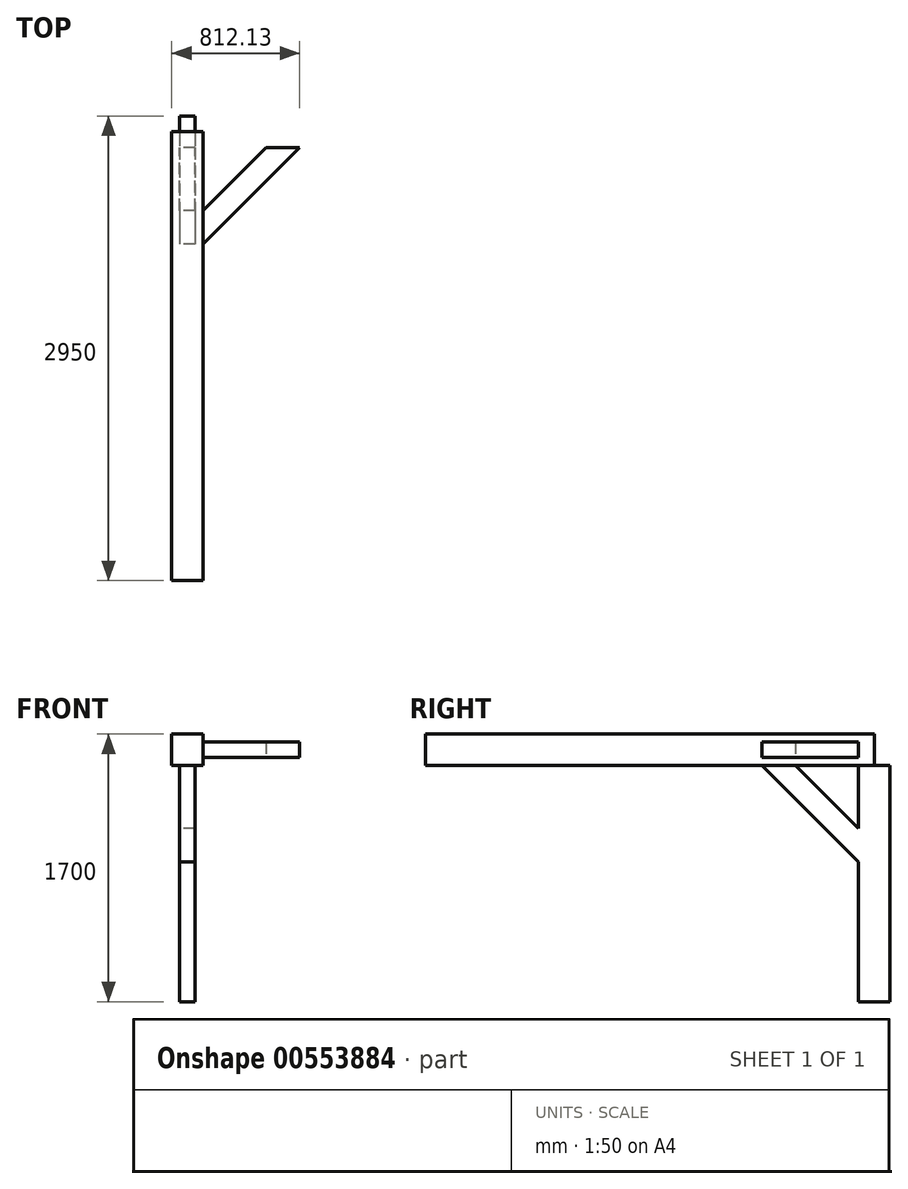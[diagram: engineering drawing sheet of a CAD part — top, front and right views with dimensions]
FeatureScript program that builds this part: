
annotation { "Feature Type Name" : "Feature", "Feature Type Description" : "" }
export const myFeature = defineFeature(function(context is Context, id is Id, definition is map)
    precondition{}
    {
        {
            var Q0;
            Q0=qCreatedBy(makeId("Top.planeOp"),FACE);
            var sketch = newSketch(context, id + "F0", { "sketchPlane" : qUnion([Q0])});
            skLineSegment(sketch, "E0", {"start": v(-358.87, -1603.5) * mm, "end": v(-158.87, -1603.5) * mm});
            skLineSegment(sketch, "E1", {"start": v(-158.87, -1603.5) * mm, "end": v(-158.87, 534.37) * mm});
            skLineSegment(sketch, "E2", {"start": v(-158.87, 534.37) * mm, "end": v(453.26, 1146.5) * mm});
            skLineSegment(sketch, "E3", {"start": v(453.26, 1146.5) * mm, "end": v(241.13, 1146.5) * mm});
            skLineSegment(sketch, "E4", {"start": v(241.13, 1146.5) * mm, "end": v(-158.87, 746.5) * mm});
            skLineSegment(sketch, "E5", {"start": v(-158.87, 746.5) * mm, "end": v(-158.87, 1246.5) * mm});
            skLineSegment(sketch, "E6", {"start": v(-158.87, 1246.5) * mm, "end": v(-358.87, 1246.5) * mm});
            skLineSegment(sketch, "E7", {"start": v(-358.87, 1246.5) * mm, "end": v(-358.87, -1603.5) * mm});
            skSolve(sketch);
        }
        {
            var Q0;
            Q0=makeQuery(id+"F0.imprint","IMPRINT",FACE,{"disambiguationData":[TD([[makeQuery(id+"F0.imprint","IMPRINT",EDGE,{"derivedFrom":sQuery(id+"F0.wireOp",EDGE,"E0")}),1.0]])]});
            extrude(context, id + "F1", {"entities" : qUnion([Q0]), "depth" : 200 * mm});
        }
        {
            var Q0;
            Q0=makeQuery(id+"F1.opExtrude","CAP_FACE",FACE,{"disambiguationData":[OSD([sQuery(id+"F0.wireOp",EDGE,"E0"),sQuery(id+"F0.wireOp",EDGE,"E1"),sQuery(id+"F0.wireOp",EDGE,"E2"),sQuery(id+"F0.wireOp",EDGE,"E3"),sQuery(id+"F0.wireOp",EDGE,"E4"),sQuery(id+"F0.wireOp",EDGE,"E5"),sQuery(id+"F0.wireOp",EDGE,"E6"),sQuery(id+"F0.wireOp",EDGE,"E7")])],"isStart":true});
            var sketch = newSketch(context, id + "F2", { "sketchPlane" : qUnion([Q0])});
            skLineSegment(sketch, "E8", {"start": v(-158.87, -534.37) * mm, "end": v(-158.87, -746.5) * mm});
            skLineSegment(sketch, "E9", {"start": v(-158.87, -746.5) * mm, "end": v(241.13, -1146.5) * mm});
            skLineSegment(sketch, "E10", {"start": v(241.13, -1146.5) * mm, "end": v(453.26, -1146.5) * mm});
            skLineSegment(sketch, "E11", {"start": v(453.26, -1146.5) * mm, "end": v(-158.87, -534.37) * mm});
            skSolve(sketch);
        }
        {
            var Q0;
            Q0=makeQuery(id+"F2.imprint","IMPRINT",FACE,{"disambiguationData":[TD([[makeQuery(id+"F2.imprint","IMPRINT",EDGE,{"derivedFrom":sQuery(id+"F2.wireOp",EDGE,"E8")}),1.0]])]});
            extrude(context, id + "F3", {"entities" : qUnion([Q0]), "operationType" : NewBodyOperationType.REMOVE, "oppositeDirection" : true, "depth" : 50 * mm});
        }
        {
            var Q0;
            Q0=makeQuery(id+"F1.opExtrude","CAP_FACE",FACE,{"disambiguationData":[OSD([sQuery(id+"F0.wireOp",EDGE,"E0"),sQuery(id+"F0.wireOp",EDGE,"E1"),sQuery(id+"F0.wireOp",EDGE,"E2"),sQuery(id+"F0.wireOp",EDGE,"E3"),sQuery(id+"F0.wireOp",EDGE,"E4"),sQuery(id+"F0.wireOp",EDGE,"E5"),sQuery(id+"F0.wireOp",EDGE,"E6"),sQuery(id+"F0.wireOp",EDGE,"E7")])],"isStart":false});
            var sketch = newSketch(context, id + "F4", { "sketchPlane" : qUnion([Q0])});
            skLineSegment(sketch, "E12", {"start": v(-158.87, 746.5) * mm, "end": v(-158.87, 534.37) * mm});
            skLineSegment(sketch, "E13", {"start": v(-158.87, 534.37) * mm, "end": v(453.26, 1146.5) * mm});
            skLineSegment(sketch, "E14", {"start": v(453.26, 1146.5) * mm, "end": v(241.13, 1146.5) * mm});
            skLineSegment(sketch, "E15", {"start": v(241.13, 1146.5) * mm, "end": v(-158.87, 746.5) * mm});
            skSolve(sketch);
        }
        {
            var Q0;
            Q0=makeQuery(id+"F4.imprint","IMPRINT",FACE,{"disambiguationData":[TD([[makeQuery(id+"F4.imprint","IMPRINT",EDGE,{"derivedFrom":sQuery(id+"F4.wireOp",EDGE,"E12")}),1.0]])]});
            extrude(context, id + "F5", {"entities" : qUnion([Q0]), "operationType" : NewBodyOperationType.REMOVE, "oppositeDirection" : true, "depth" : 50 * mm});
        }
        {
            var Q0;
            Q0=makeQuery(id+"F1.opExtrude","SWEPT_FACE",FACE,{"disambiguationData":[OSD([sQuery(id+"F0.wireOp",EDGE,"E7")])]});
            cPlane(context, id + "F6", {"entities" : qUnion([Q0]), "cplaneType" : CPlaneType.OFFSET, "offset" : 50 * mm, "oppositeDirection" : true, "width" : 150 * mm, "height" : 150 * mm});
        }
        {
            var Q0;
            Q0=qCreatedBy(id+"F6.planeOp",FACE);
            var sketch = newSketch(context, id + "F7", { "sketchPlane" : qUnion([Q0])});
            skLineSegment(sketch, "E16.0", {"start": v(-1246.5, 0) * mm, "end": v(1603.5, 0) * mm});
            skLineSegment(sketch, "E17", {"start": v(-746.5, 0) * mm, "end": v(-1146.5, -400) * mm});
            skLineSegment(sketch, "E18", {"start": v(-1146.5, -400) * mm, "end": v(-1146.5, -612.13) * mm});
            skLineSegment(sketch, "E19", {"start": v(-1146.5, -612.13) * mm, "end": v(-534.37, 0) * mm});
            skLineSegment(sketch, "E20", {"start": v(-534.37, 0) * mm, "end": v(-746.5, 0) * mm});
            skSolve(sketch);
        }
        {
            var Q0;
            Q0=makeQuery(id+"F7.imprint","IMPRINT",FACE,{"disambiguationData":[TD([[makeQuery(id+"F7.imprint","IMPRINT",EDGE,{"derivedFrom":sQuery(id+"F7.wireOp",EDGE,"E17")}),1.0]])]});
            extrude(context, id + "F8", {"entities" : qUnion([Q0]), "operationType" : NewBodyOperationType.ADD, "oppositeDirection" : true, "depth" : 100 * mm});
        }
        {
            var Q0;
            Q0=makeQuery(id+"F8.opExtrude","SWEPT_FACE",FACE,{"disambiguationData":[OSD([sQuery(id+"F7.wireOp",EDGE,"E18")])]});
            var sketch = newSketch(context, id + "F9", { "sketchPlane" : qUnion([Q0])});
            skLineSegment(sketch, "E21.bottom", {"start": v(208.87, -1500) * mm, "end": v(308.87, -1500) * mm});
            skLineSegment(sketch, "E21.top", {"start": v(208.87, 0) * mm, "end": v(308.87, 0) * mm});
            skLineSegment(sketch, "E21.left", {"start": v(208.87, -1500) * mm, "end": v(208.87, 0) * mm});
            skLineSegment(sketch, "E21.right", {"start": v(308.87, -1500) * mm, "end": v(308.87, 0) * mm});
            skSolve(sketch);
        }
        {
            var Q0;
            {var subQ0=sQuery(id+"F9.wireOp",EDGE,"E21.bottom");Q0=makeQuery(id+"F9.imprint","IMPRINT",FACE,{"disambiguationData":[TD([[makeQuery(id+"F9.imprint","IMPRINT",EDGE,{"derivedFrom":subQ0}),1.0]])]});}
            var Q1;
            {var subQ1=sQuery(id+"F7.wireOp",EDGE,"E18");var subQ2=makeQuery(id+"F8.opExtrude","SWEPT_EDGE",EDGE,{"disambiguationData":[OSD([sQuery(id+"F7.wireOp",EDGE,"E17"),subQ1])]});Q1=makeQuery(id+"F9.imprint","IMPRINT",FACE,{"disambiguationData":[TD([[makeQuery(id+"F9.imprint","IMPRINT",EDGE,{"derivedFrom":subQ2}),-1.0]])]});}
            var Q2;
            {var subQ0=sQuery(id+"F9.wireOp",EDGE,"E21.top");Q2=makeQuery(id+"F9.imprint","IMPRINT",FACE,{"disambiguationData":[TD([[makeQuery(id+"F9.imprint","IMPRINT",EDGE,{"derivedFrom":subQ0}),-1.0]])]});}
            extrude(context, id + "F10", {"entities" : qUnion([Q0, Q1, Q2]), "operationType" : NewBodyOperationType.ADD, "depth" : 200 * mm});
        }
    });
